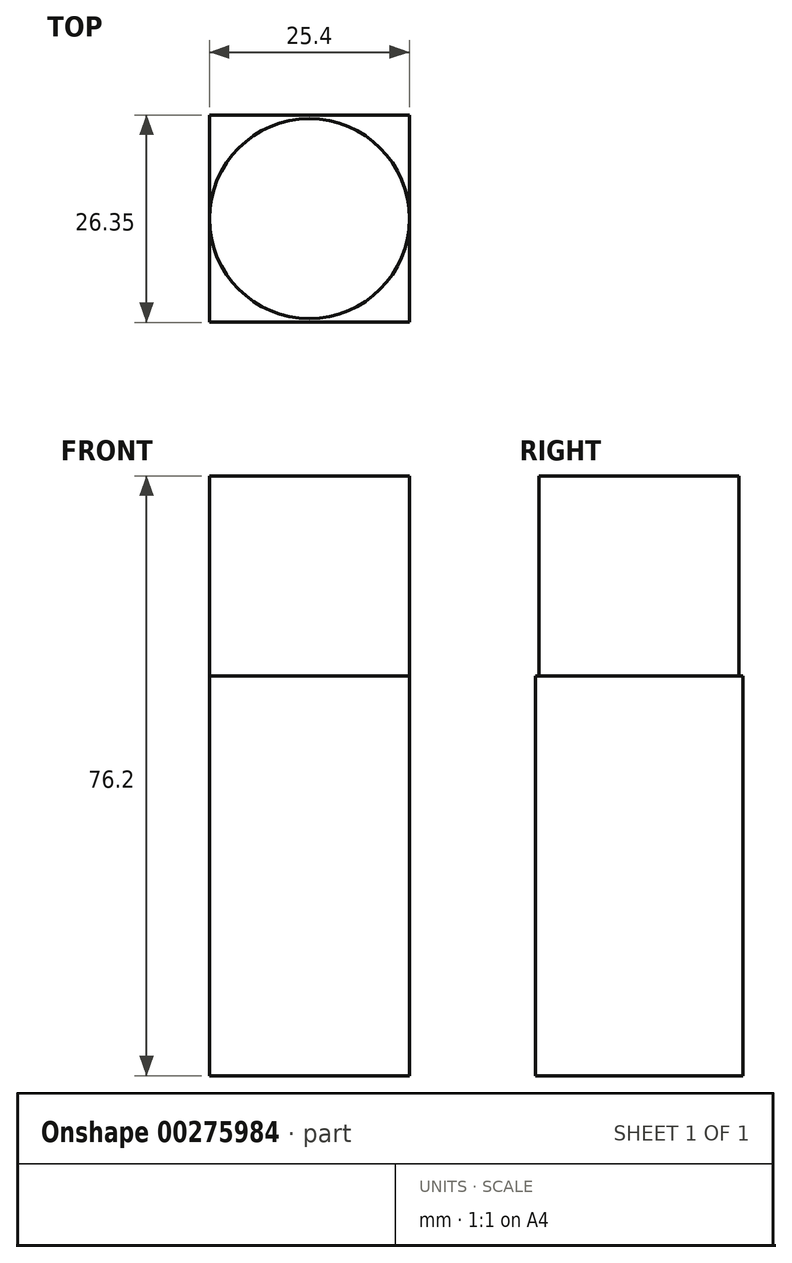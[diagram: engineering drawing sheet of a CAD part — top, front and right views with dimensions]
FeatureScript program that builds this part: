
annotation { "Feature Type Name" : "Feature", "Feature Type Description" : "" }
export const myFeature = defineFeature(function(context is Context, id is Id, definition is map)
    precondition{}
    {
        {
            var Q0;
            Q0=qCreatedBy(makeId("Top.planeOp"),FACE);
            var sketch = newSketch(context, id + "F0", { "sketchPlane" : qUnion([Q0])});
            skLineSegment(sketch, "E0.bottom", {"start": v(-57, -57.16) * mm, "end": v(-31.6, -57.16) * mm});
            skLineSegment(sketch, "E0.top", {"start": v(-57, -30.81) * mm, "end": v(-31.6, -30.81) * mm});
            skLineSegment(sketch, "E0.left", {"start": v(-57, -57.16) * mm, "end": v(-57, -30.81) * mm});
            skLineSegment(sketch, "E0.right", {"start": v(-31.6, -57.16) * mm, "end": v(-31.6, -30.81) * mm});
            skSolve(sketch);
        }
        {
            var Q0;
            Q0=makeQuery(id+"F0.imprint","IMPRINT",FACE,{"disambiguationData":[TD([[makeQuery(id+"F0.imprint","IMPRINT",EDGE,{"derivedFrom":sQuery(id+"F0.wireOp",EDGE,"E0.bottom")}),1.0]])]});
            extrude(context, id + "F1", {"entities" : qUnion([Q0]), "depth" : 50.8 * mm});
        }
        {
            var Q0;
            Q0=makeQuery(id+"F1.opExtrude","CAP_FACE",FACE,{"disambiguationData":[OSD([sQuery(id+"F0.wireOp",EDGE,"E0.bottom"),sQuery(id+"F0.wireOp",EDGE,"E0.top"),sQuery(id+"F0.wireOp",EDGE,"E0.left"),sQuery(id+"F0.wireOp",EDGE,"E0.right")])],"isStart":false});
            var sketch = newSketch(context, id + "F2", { "sketchPlane" : qUnion([Q0])});
            skLineSegment(sketch, "E1", {"start": v(-44.3, -30.81) * mm, "end": v(-44.3, -57.16) * mm});
            skLineSegment(sketch, "E2", {"start": v(-57, -43.99) * mm, "end": v(-31.6, -43.99) * mm});
            skCircle(sketch, "E3", {"center": v(-44.3, -43.99) * mm, "radius": 12.7 * mm});
            skSolve(sketch);
        }
        {
            var Q0;
            {var subQ0=sQuery(id+"F2.wireOp",EDGE,"E2");var subQ1=sQuery(id+"F2.wireOp",EDGE,"E1");var subQ2=makeQuery(id+"F2.imprint","INTERSECT",VERTEX,{"derivedFrom":[subQ1,subQ0]});Q0=makeQuery(id+"F2.imprint","IMPRINT",FACE,{"disambiguationData":[TD([[makeQuery(id+"F2.imprint","IMPRINT",EDGE,{"disambiguationData":[TD([[subQ2,-1.0]])],"derivedFrom":subQ1}),1.0]])]});}
            var Q1;
            {var subQ0=sQuery(id+"F2.wireOp",EDGE,"E3");var subQ1=sQuery(id+"F2.wireOp",EDGE,"E1");var subQ2=makeQuery(id+"F2.imprint","INTERSECT",VERTEX,{"disambiguationData":[OD(0.0)],"derivedFrom":[subQ1,subQ0]});Q1=makeQuery(id+"F2.imprint","IMPRINT",FACE,{"disambiguationData":[TD([[makeQuery(id+"F2.imprint","IMPRINT",EDGE,{"disambiguationData":[TD([[subQ2,-1.0]])],"derivedFrom":subQ1}),1.0]])]});}
            var Q2;
            {var subQ0=sQuery(id+"F2.wireOp",EDGE,"E3");var subQ1=sQuery(id+"F2.wireOp",EDGE,"E1");var subQ2=makeQuery(id+"F2.imprint","INTERSECT",VERTEX,{"disambiguationData":[OD(0.0)],"derivedFrom":[subQ1,subQ0]});Q2=makeQuery(id+"F2.imprint","IMPRINT",FACE,{"disambiguationData":[TD([[makeQuery(id+"F2.imprint","IMPRINT",EDGE,{"disambiguationData":[TD([[subQ2,-1.0]])],"derivedFrom":subQ1}),-1.0]])]});}
            var Q3;
            {var subQ0=sQuery(id+"F2.wireOp",EDGE,"E2");var subQ1=sQuery(id+"F2.wireOp",EDGE,"E1");var subQ2=makeQuery(id+"F2.imprint","INTERSECT",VERTEX,{"derivedFrom":[subQ1,subQ0]});Q3=makeQuery(id+"F2.imprint","IMPRINT",FACE,{"disambiguationData":[TD([[makeQuery(id+"F2.imprint","IMPRINT",EDGE,{"disambiguationData":[TD([[subQ2,-1.0]])],"derivedFrom":subQ1}),-1.0]])]});}
            extrude(context, id + "F3", {"entities" : qUnion([Q0, Q1, Q2, Q3]), "operationType" : NewBodyOperationType.ADD, "depth" : 25.4 * mm});
        }
    });
